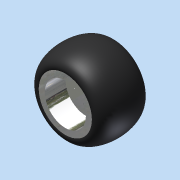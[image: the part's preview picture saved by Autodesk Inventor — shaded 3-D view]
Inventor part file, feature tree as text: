
AUTODESK INVENTOR PART (.ipt)
format: ipt  version: 2011 SP1 (Build 150282100, 282)  size: 294,912 bytes
history: native  units: in
note: dims shown in document units (in); Inventor stores cm internally (conversion verified against a paired STEP export)
features: sketch x8, extrude x7, projected_geometry x3, revolve x1
ambient origin geometry x8: Origin, YZ Plane, XZ Plane, XY Plane, X Axis, Y Axis, Z Axis, Center Point
bodies: Solid1 (feature_tree)
feature tree (19):
  extrude  "Extrusion1"  Depth=2.84in
  extrude  "Extrusion2"  Depth=0.326in TaperAngle=0.0deg
  extrude  "Extrusion3"  Depth=0.15in
  extrude  "Extrusion4"  Depth=2.6in
  extrude  "Extrusion5"  Depth=0.3in
  extrude  "Extrusion6"  Depth=1.33in
  revolve  "Revolution1"  [1 undecoded]
  extrude  "Extrusion7"  Depth=1.1811in TaperAngle=360.0deg
  sketch  "Sketch1"  dims[d0=2.6in d1=2.84in]
  sketch  "Sketch2"  dims[d2=1.48in d3=0.0in d4=0.326in d5=0.0in]
  sketch  "Sketch3"  dims[d6=0.824in d7=0.15in]
  sketch  "Sketch4"  dims[d8=0.31in d9=0.0in d10=2.6in]
  sketch  "Sketch5"  dims[d11=1.314in d12=0.0in d13=0.3in]
  sketch  "Sketch6"  dims[d14=0.41in d15=0.0in d16=1.33in]
  sketch  "Sketch7"  dims[d17=0.05in d18=0.05in]
  sketch  "Sketch8"  dims[d19=0.025in d20=1.1811in d22=360.0deg d24=0.32in d25=0.0in d26=0.26in d27=0.26in d31=5.0in d32=90.0deg d33=0.375in d34=0.6575in d35=3.1496in d37=360.0deg d39=0.21in d40=0.0in]
  projected_geometry  "Project Cut Edges1"
  projected_geometry  "Project Cut Edges2"
  projected_geometry  "Project Cut Edges3"
note: 1 required parameter value undecoded (feature->parameter linkage not recoverable at this tier; creation-order binding heuristic only, values carry confidence <= 0.55)
